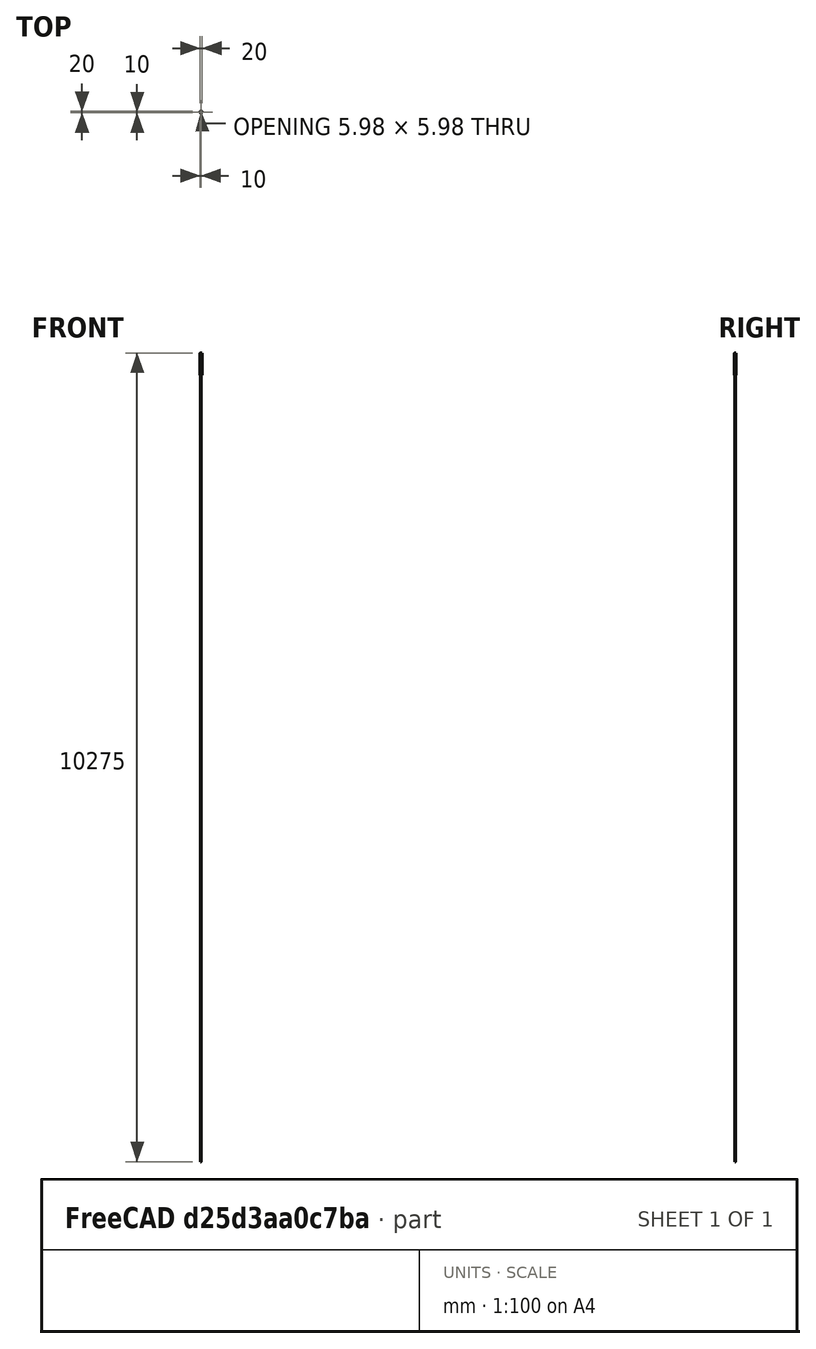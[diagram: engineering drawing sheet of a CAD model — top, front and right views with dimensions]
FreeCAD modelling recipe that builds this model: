
FCSTD DOCUMENT  (FreeCAD 0.15R4671 (Git))
Label: perfil 280mm
License: CC-BY 3.0
LicenseURL: http://creativecommons.org/licenses/by/3.0/
objects: Sketcher::SketchObject×2, Part::Extrusion×2, PartDesign::Pad×1, PartDesign::Pocket×1, App::MeasureDistance×1, Part::Cut×1
note: 9 computed .brp shape members not serialized (recipe doc carries the construction recipe); baked Part::Feature solids carry a one-line shape summary decoded from their .brp

FEATURE [Sketcher::SketchObject] Sketch
  Placement = pos=(1.5,0,0) rot=(0,0,1;0rad)
  sketch-geometry (136):
    g0: LineSegment StartX=0 StartY=20 StartZ=0 EndX=4.65 EndY=20 EndZ=0
    g1: ArcOfCircle CenterX=-1e-12 CenterY=18.5 CenterZ=0 NormalX=0 NormalY=0 NormalZ=1 Radius=1.5 StartAngle=1.5708 EndAngle=3.14159
    g2: LineSegment StartX=-1.5 StartY=13.85 StartZ=0 EndX=-1.5 EndY=18.5 EndZ=0
    g3: ArcOfCircle CenterX=-1.3 CenterY=13.85 CenterZ=0 NormalX=0 NormalY=0 NormalZ=1 Radius=0.2 StartAngle=3.14159 EndAngle=4.71239
    g4: LineSegment StartX=-1 StartY=13.65 StartZ=0 EndX=-1.3 EndY=13.65 EndZ=0
    g5: LineSegment StartX=-1 StartY=13.3 StartZ=0 EndX=-1 EndY=13.65 EndZ=0
    g6: ArcOfCircle CenterX=-0.8 CenterY=13.3 CenterZ=0 NormalX=0 NormalY=0 NormalZ=1 Radius=0.2 StartAngle=3.14159 EndAngle=4.71239
    g7: LineSegment StartX=-0.5 StartY=13.1 StartZ=0 EndX=-0.8 EndY=13.1 EndZ=0
    g8: ArcOfCircle CenterX=-0.5 CenterY=13.6 CenterZ=0 NormalX=0 NormalY=0 NormalZ=1 Radius=0.5 StartAngle=4.71239 EndAngle=6.28319
    g9: LineSegment StartX=2.68e-07 StartY=15.5 StartZ=0 EndX=2.68e-07 EndY=13.6 EndZ=0
    g10: ArcOfCircle CenterX=0.5 CenterY=15.5 CenterZ=0 NormalX=0 NormalY=0 NormalZ=1 Radius=0.5 StartAngle=1.5708 EndAngle=3.14159
    g11: LineSegment StartX=1.23223 StartY=16 StartZ=0 EndX=0.5 EndY=16 EndZ=0
    g12: ArcOfCircle CenterX=1.23223 CenterY=15.5 CenterZ=0 NormalX=0 NormalY=0 NormalZ=1 Radius=0.5 StartAngle=0.785398 EndAngle=1.5708
    g13: LineSegment StartX=3.85355 StartY=13.5858 StartZ=0 EndX=1.58579 EndY=15.8536 EndZ=0
    g14: ArcOfCircle CenterX=3.5 CenterY=13.2322 CenterZ=0 NormalX=0 NormalY=0 NormalZ=1 Radius=0.5 StartAngle=0 EndAngle=0.785398
    g15: LineSegment StartX=4 StartY=10.9536 StartZ=0 EndX=4 EndY=13.2322 EndZ=0
    g16: ArcOfCircle CenterX=4.2 CenterY=10.9536 CenterZ=0 NormalX=0 NormalY=0 NormalZ=1 Radius=0.2 StartAngle=3.14159 EndAngle=3.66519
    g17: LineSegment StartX=4.46188 StartY=10.1 StartZ=0 EndX=4.0268 EndY=10.8536 EndZ=0
    g18: ArcOfCircle CenterX=4.28868 CenterY=10 CenterZ=0 NormalX=0 NormalY=0 NormalZ=1 Radius=0.2 StartAngle=5.75959 EndAngle=6.80678
    g19: LineSegment StartX=4.0268 StartY=9.14641 StartZ=0 EndX=4.46188 EndY=9.9 EndZ=0
    g20: ArcOfCircle CenterX=4.2 CenterY=9.04641 CenterZ=0 NormalX=0 NormalY=0 NormalZ=1 Radius=0.2 StartAngle=2.61799 EndAngle=3.14159
    g21: LineSegment StartX=4 StartY=6.76777 StartZ=0 EndX=4 EndY=9.04641 EndZ=0
    g22: ArcOfCircle CenterX=3.5 CenterY=6.76777 CenterZ=0 NormalX=0 NormalY=0 NormalZ=1 Radius=0.5 StartAngle=5.49779 EndAngle=6.28319
    g23: LineSegment StartX=1.58579 StartY=4.14645 StartZ=0 EndX=3.85355 EndY=6.41421 EndZ=0
    g24: ArcOfCircle CenterX=1.23223 CenterY=4.5 CenterZ=0 NormalX=0 NormalY=0 NormalZ=1 Radius=0.5 StartAngle=4.71239 EndAngle=5.49779
    g25: LineSegment StartX=0.5 StartY=4 StartZ=0 EndX=1.23223 EndY=4 EndZ=0
    g26: ArcOfCircle CenterX=0.5 CenterY=4.5 CenterZ=0 NormalX=0 NormalY=0 NormalZ=1 Radius=0.5 StartAngle=3.14159 EndAngle=4.71239
    g27: LineSegment StartX=2.68e-07 StartY=6.4 StartZ=0 EndX=2.68e-07 EndY=4.5 EndZ=0
    g28: ArcOfCircle CenterX=-0.5 CenterY=6.4 CenterZ=0 NormalX=0 NormalY=0 NormalZ=1 Radius=0.5 StartAngle=0 EndAngle=1.5708
    g29: LineSegment StartX=-0.8 StartY=6.9 StartZ=0 EndX=-0.5 EndY=6.9 EndZ=0
    g30: ArcOfCircle CenterX=-0.8 CenterY=6.7 CenterZ=0 NormalX=0 NormalY=0 NormalZ=1 Radius=0.2 StartAngle=1.5708 EndAngle=3.14159
    g31: LineSegment StartX=-1 StartY=6.35 StartZ=0 EndX=-1 EndY=6.7 EndZ=0
    g32: LineSegment StartX=-1.3 StartY=6.35 StartZ=0 EndX=-1 EndY=6.35 EndZ=0
    g33: ArcOfCircle CenterX=-1.3 CenterY=6.15 CenterZ=0 NormalX=0 NormalY=0 NormalZ=1 Radius=0.2 StartAngle=1.5708 EndAngle=3.14159
    g34: LineSegment StartX=-1.5 StartY=1.5 StartZ=0 EndX=-1.5 EndY=6.15 EndZ=0
    g35: ArcOfCircle CenterX=0 CenterY=1.5 CenterZ=0 NormalX=0 NormalY=0 NormalZ=1 Radius=1.5 StartAngle=3.14159 EndAngle=4.71239
    g36: LineSegment StartX=4.65 StartY=1e-12 StartZ=0 EndX=0 EndY=0 EndZ=0
    g37: ArcOfCircle CenterX=4.65 CenterY=0.2 CenterZ=0 NormalX=0 NormalY=0 NormalZ=1 Radius=0.2 StartAngle=4.71239 EndAngle=6.28319
    g38: LineSegment StartX=4.85 StartY=0.5 StartZ=0 EndX=4.85 EndY=0.2 EndZ=0
    g39: LineSegment StartX=5.2 StartY=0.5 StartZ=0 EndX=4.85 EndY=0.5 EndZ=0
    g40: ArcOfCircle CenterX=5.2 CenterY=0.7 CenterZ=0 NormalX=0 NormalY=0 NormalZ=1 Radius=0.2 StartAngle=4.71239 EndAngle=6.28319
    g41: LineSegment StartX=5.4 StartY=1 StartZ=0 EndX=5.4 EndY=0.7 EndZ=0
    g42: ArcOfCircle CenterX=4.9 CenterY=1 CenterZ=0 NormalX=0 NormalY=0 NormalZ=1 Radius=0.5 StartAngle=0 EndAngle=1.5708
    g43: LineSegment StartX=3 StartY=1.5 StartZ=0 EndX=4.9 EndY=1.5 EndZ=0
    g44: ArcOfCircle CenterX=3 CenterY=2 CenterZ=0 NormalX=0 NormalY=0 NormalZ=1 Radius=0.5 StartAngle=3.14159 EndAngle=4.71239
    g45: LineSegment StartX=2.5 StartY=2.73223 StartZ=0 EndX=2.5 EndY=2 EndZ=0
    g46: ArcOfCircle CenterX=3 CenterY=2.73223 CenterZ=0 NormalX=0 NormalY=0 NormalZ=1 Radius=0.5 StartAngle=2.35619 EndAngle=3.14159
    g47: LineSegment StartX=4.91421 StartY=5.35355 StartZ=0 EndX=2.64645 EndY=3.08579 EndZ=0
    g48: ArcOfCircle CenterX=5.26777 CenterY=5 CenterZ=0 NormalX=0 NormalY=0 NormalZ=1 Radius=0.5 StartAngle=1.5708 EndAngle=2.35619
    g49: LineSegment StartX=7.54641 StartY=5.5 StartZ=0 EndX=5.26777 EndY=5.5 EndZ=0
    g50: ArcOfCircle CenterX=7.54641 CenterY=5.7 CenterZ=0 NormalX=0 NormalY=0 NormalZ=1 Radius=0.2 StartAngle=4.71239 EndAngle=5.23599
    g51: LineSegment StartX=8.4 StartY=5.96188 StartZ=0 EndX=7.64641 EndY=5.52679 EndZ=0
    g52: ArcOfCircle CenterX=8.5 CenterY=5.78868 CenterZ=0 NormalX=0 NormalY=0 NormalZ=1 Radius=0.2 StartAngle=1.0472 EndAngle=2.0944
    g53: LineSegment StartX=9.35359 StartY=5.52679 StartZ=0 EndX=8.6 EndY=5.96188 EndZ=0
    g54: ArcOfCircle CenterX=9.45359 CenterY=5.7 CenterZ=0 NormalX=0 NormalY=0 NormalZ=1 Radius=0.2 StartAngle=4.18879 EndAngle=4.71239
    g55: LineSegment StartX=11.7322 StartY=5.5 StartZ=0 EndX=9.45359 EndY=5.5 EndZ=0
    g56: ArcOfCircle CenterX=11.7322 CenterY=5 CenterZ=0 NormalX=0 NormalY=0 NormalZ=1 Radius=0.5 StartAngle=0.785398 EndAngle=1.5708
    g57: LineSegment StartX=14.3536 StartY=3.08579 StartZ=0 EndX=12.0858 EndY=5.35355 EndZ=0
    g58: ArcOfCircle CenterX=14 CenterY=2.73223 CenterZ=0 NormalX=0 NormalY=0 NormalZ=1 Radius=0.5 StartAngle=0 EndAngle=0.785398
    g59: LineSegment StartX=14.5 StartY=2 StartZ=0 EndX=14.5 EndY=2.73223 EndZ=0
    g60: ArcOfCircle CenterX=14 CenterY=2 CenterZ=0 NormalX=0 NormalY=0 NormalZ=1 Radius=0.5 StartAngle=4.71239 EndAngle=6.28319
    g61: LineSegment StartX=12.1 StartY=1.5 StartZ=0 EndX=14 EndY=1.5 EndZ=0
    g62: ArcOfCircle CenterX=12.1 CenterY=1 CenterZ=0 NormalX=0 NormalY=0 NormalZ=1 Radius=0.5 StartAngle=1.5708 EndAngle=3.14159
    g63: LineSegment StartX=11.6 StartY=0.7 StartZ=0 EndX=11.6 EndY=1 EndZ=0
    g64: ArcOfCircle CenterX=11.8 CenterY=0.7 CenterZ=0 NormalX=0 NormalY=0 NormalZ=1 Radius=0.2 StartAngle=3.14159 EndAngle=4.71239
    g65: LineSegment StartX=12.15 StartY=0.5 StartZ=0 EndX=11.8 EndY=0.5 EndZ=0
    g66: LineSegment StartX=12.15 StartY=0.2 StartZ=0 EndX=12.15 EndY=0.5 EndZ=0
    g67: ArcOfCircle CenterX=12.35 CenterY=0.2 CenterZ=0 NormalX=0 NormalY=0 NormalZ=1 Radius=0.2 StartAngle=3.14159 EndAngle=4.71239
    g68: LineSegment StartX=17 StartY=1e-12 StartZ=0 EndX=12.35 EndY=0 EndZ=0
    g69: ArcOfCircle CenterX=17 CenterY=1.5 CenterZ=0 NormalX=0 NormalY=0 NormalZ=1 Radius=1.5 StartAngle=4.71239 EndAngle=6.28319
    g70: LineSegment StartX=18.5 StartY=6.15 StartZ=0 EndX=18.5 EndY=1.5 EndZ=0
    g71: ArcOfCircle CenterX=18.3 CenterY=6.15 CenterZ=0 NormalX=0 NormalY=0 NormalZ=1 Radius=0.2 StartAngle=0 EndAngle=1.5708
    g72: LineSegment StartX=18 StartY=6.35 StartZ=0 EndX=18.3 EndY=6.35 EndZ=0
    g73: LineSegment StartX=18 StartY=6.7 StartZ=0 EndX=18 EndY=6.35 EndZ=0
    g74: ArcOfCircle CenterX=17.8 CenterY=6.7 CenterZ=0 NormalX=0 NormalY=0 NormalZ=1 Radius=0.2 StartAngle=0 EndAngle=1.5708
    g75: LineSegment StartX=17.5 StartY=6.9 StartZ=0 EndX=17.8 EndY=6.9 EndZ=0
    g76: ArcOfCircle CenterX=17.5 CenterY=6.4 CenterZ=0 NormalX=0 NormalY=0 NormalZ=1 Radius=0.5 StartAngle=1.5708 EndAngle=3.14159
    g77: LineSegment StartX=17 StartY=4.5 StartZ=0 EndX=17 EndY=6.4 EndZ=0
    g78: ArcOfCircle CenterX=16.5 CenterY=4.5 CenterZ=0 NormalX=0 NormalY=0 NormalZ=1 Radius=0.5 StartAngle=4.71239 EndAngle=6.28319
    g79: LineSegment StartX=15.7678 StartY=4 StartZ=0 EndX=16.5 EndY=4 EndZ=0
    g80: ArcOfCircle CenterX=15.7678 CenterY=4.5 CenterZ=0 NormalX=0 NormalY=0 NormalZ=1 Radius=0.5 StartAngle=3.92699 EndAngle=4.71239
    g81: LineSegment StartX=13.1464 StartY=6.41421 StartZ=0 EndX=15.4142 EndY=4.14645 EndZ=0
    g82: ArcOfCircle CenterX=13.5 CenterY=6.76777 CenterZ=0 NormalX=0 NormalY=0 NormalZ=1 Radius=0.5 StartAngle=3.14159 EndAngle=3.92699
    g83: LineSegment StartX=13 StartY=9.04641 StartZ=0 EndX=13 EndY=6.76777 EndZ=0
    g84: ArcOfCircle CenterX=12.8 CenterY=9.04641 CenterZ=0 NormalX=0 NormalY=0 NormalZ=1 Radius=0.2 StartAngle=0 EndAngle=0.523599
    g85: LineSegment StartX=12.5381 StartY=9.9 StartZ=0 EndX=12.9732 EndY=9.14641 EndZ=0
    g86: ArcOfCircle CenterX=12.7113 CenterY=10 CenterZ=0 NormalX=0 NormalY=0 NormalZ=1 Radius=0.2 StartAngle=2.61799 EndAngle=3.66519
    g87: LineSegment StartX=12.9732 StartY=10.8536 StartZ=0 EndX=12.5381 EndY=10.1 EndZ=0
    g88: ArcOfCircle CenterX=12.8 CenterY=10.9536 CenterZ=0 NormalX=0 NormalY=0 NormalZ=1 Radius=0.2 StartAngle=5.75959 EndAngle=6.28319
    g89: LineSegment StartX=13 StartY=13.2322 StartZ=0 EndX=13 EndY=10.9536 EndZ=0
    g90: ArcOfCircle CenterX=13.5 CenterY=13.2322 CenterZ=0 NormalX=0 NormalY=0 NormalZ=1 Radius=0.5 StartAngle=2.35619 EndAngle=3.14159
    g91: LineSegment StartX=15.4142 StartY=15.8536 StartZ=0 EndX=13.1464 EndY=13.5858 EndZ=0
    g92: ArcOfCircle CenterX=15.7678 CenterY=15.5 CenterZ=0 NormalX=0 NormalY=0 NormalZ=1 Radius=0.5 StartAngle=1.5708 EndAngle=2.35619
    g93: LineSegment StartX=16.5 StartY=16 StartZ=0 EndX=15.7678 EndY=16 EndZ=0
    g94: ArcOfCircle CenterX=16.5 CenterY=15.5 CenterZ=0 NormalX=0 NormalY=0 NormalZ=1 Radius=0.5 StartAngle=0 EndAngle=1.5708
    g95: LineSegment StartX=17 StartY=13.6 StartZ=0 EndX=17 EndY=15.5 EndZ=0
    g96: ArcOfCircle CenterX=17.5 CenterY=13.6 CenterZ=0 NormalX=0 NormalY=0 NormalZ=1 Radius=0.5 StartAngle=3.14159 EndAngle=4.71239
    g97: LineSegment StartX=17.8 StartY=13.1 StartZ=0 EndX=17.5 EndY=13.1 EndZ=0
    g98: ArcOfCircle CenterX=17.8 CenterY=13.3 CenterZ=0 NormalX=0 NormalY=0 NormalZ=1 Radius=0.2 StartAngle=4.71239 EndAngle=6.28319
    g99: LineSegment StartX=18 StartY=13.65 StartZ=0 EndX=18 EndY=13.3 EndZ=0
    g100: LineSegment StartX=18.3 StartY=13.65 StartZ=0 EndX=18 EndY=13.65 EndZ=0
    g101: ArcOfCircle CenterX=18.3 CenterY=13.85 CenterZ=0 NormalX=0 NormalY=0 NormalZ=1 Radius=0.2 StartAngle=4.71239 EndAngle=6.28319
    g102: LineSegment StartX=18.5 StartY=18.5 StartZ=0 EndX=18.5 EndY=13.85 EndZ=0
    g103: ArcOfCircle CenterX=17 CenterY=18.5 CenterZ=0 NormalX=0 NormalY=0 NormalZ=1 Radius=1.5 StartAngle=0 EndAngle=1.5708
    g104: LineSegment StartX=12.35 StartY=20 StartZ=0 EndX=17 EndY=20 EndZ=0
    g105: ArcOfCircle CenterX=12.35 CenterY=19.8 CenterZ=0 NormalX=0 NormalY=0 NormalZ=1 Radius=0.2 StartAngle=1.5708 EndAngle=3.14159
    g106: LineSegment StartX=12.15 StartY=19.5 StartZ=0 EndX=12.15 EndY=19.8 EndZ=0
    g107: LineSegment StartX=11.8 StartY=19.5 StartZ=0 EndX=12.15 EndY=19.5 EndZ=0
    g108: ArcOfCircle CenterX=11.8 CenterY=19.3 CenterZ=0 NormalX=0 NormalY=0 NormalZ=1 Radius=0.2 StartAngle=1.5708 EndAngle=3.14159
    g109: LineSegment StartX=11.6 StartY=19 StartZ=0 EndX=11.6 EndY=19.3 EndZ=0
    g110: ArcOfCircle CenterX=12.1 CenterY=19 CenterZ=0 NormalX=0 NormalY=0 NormalZ=1 Radius=0.5 StartAngle=3.14159 EndAngle=4.71239
    g111: LineSegment StartX=14 StartY=18.5 StartZ=0 EndX=12.1 EndY=18.5 EndZ=0
    g112: ArcOfCircle CenterX=14 CenterY=18 CenterZ=0 NormalX=0 NormalY=0 NormalZ=1 Radius=0.5 StartAngle=0 EndAngle=1.5708
    g113: LineSegment StartX=14.5 StartY=17.2678 StartZ=0 EndX=14.5 EndY=18 EndZ=0
    g114: ArcOfCircle CenterX=14 CenterY=17.2678 CenterZ=0 NormalX=0 NormalY=0 NormalZ=1 Radius=0.5 StartAngle=5.49779 EndAngle=6.28319
    g115: LineSegment StartX=12.0858 StartY=14.6464 StartZ=0 EndX=14.3536 EndY=16.9142 EndZ=0
    g116: ArcOfCircle CenterX=11.7322 CenterY=15 CenterZ=0 NormalX=0 NormalY=0 NormalZ=1 Radius=0.5 StartAngle=4.71239 EndAngle=5.49779
    g117: LineSegment StartX=9.45359 StartY=14.5 StartZ=0 EndX=11.7322 EndY=14.5 EndZ=0
    g118: ArcOfCircle CenterX=9.45359 CenterY=14.3 CenterZ=0 NormalX=0 NormalY=0 NormalZ=1 Radius=0.2 StartAngle=1.5708 EndAngle=2.0944
    g119: LineSegment StartX=8.6 StartY=14.0381 StartZ=0 EndX=9.35359 EndY=14.4732 EndZ=0
    g120: ArcOfCircle CenterX=8.5 CenterY=14.2113 CenterZ=0 NormalX=0 NormalY=0 NormalZ=1 Radius=0.2 StartAngle=4.18879 EndAngle=5.23599
    g121: LineSegment StartX=7.64641 StartY=14.4732 StartZ=0 EndX=8.4 EndY=14.0381 EndZ=0
    g122: ArcOfCircle CenterX=7.54641 CenterY=14.3 CenterZ=0 NormalX=0 NormalY=0 NormalZ=1 Radius=0.2 StartAngle=1.0472 EndAngle=1.5708
    g123: LineSegment StartX=5.26777 StartY=14.5 StartZ=0 EndX=7.54641 EndY=14.5 EndZ=0
    g124: ArcOfCircle CenterX=5.26777 CenterY=15 CenterZ=0 NormalX=0 NormalY=0 NormalZ=1 Radius=0.5 StartAngle=3.92699 EndAngle=4.71239
    g125: LineSegment StartX=2.64645 StartY=16.9142 StartZ=0 EndX=4.91421 EndY=14.6464 EndZ=0
    g126: ArcOfCircle CenterX=3 CenterY=17.2678 CenterZ=0 NormalX=0 NormalY=0 NormalZ=1 Radius=0.5 StartAngle=3.14159 EndAngle=3.92699
    g127: LineSegment StartX=2.5 StartY=18 StartZ=0 EndX=2.5 EndY=17.2678 EndZ=0
    g128: ArcOfCircle CenterX=3 CenterY=18 CenterZ=0 NormalX=0 NormalY=0 NormalZ=1 Radius=0.5 StartAngle=1.5708 EndAngle=3.14159
    g129: LineSegment StartX=4.9 StartY=18.5 StartZ=0 EndX=3 EndY=18.5 EndZ=0
    g130: ArcOfCircle CenterX=4.9 CenterY=19 CenterZ=0 NormalX=0 NormalY=0 NormalZ=1 Radius=0.5 StartAngle=4.71239 EndAngle=6.28319
    g131: LineSegment StartX=5.4 StartY=19.3 StartZ=0 EndX=5.4 EndY=19 EndZ=0
    g132: ArcOfCircle CenterX=5.2 CenterY=19.3 CenterZ=0 NormalX=0 NormalY=0 NormalZ=1 Radius=0.2 StartAngle=0 EndAngle=1.5708
    g133: LineSegment StartX=4.85 StartY=19.5 StartZ=0 EndX=5.2 EndY=19.5 EndZ=0
    g134: LineSegment StartX=4.85 StartY=19.8 StartZ=0 EndX=4.85 EndY=19.5 EndZ=0
    g135: ArcOfCircle CenterX=4.65 CenterY=19.8 CenterZ=0 NormalX=0 NormalY=0 NormalZ=1 Radius=0.2 StartAngle=0 EndAngle=1.5708
  constraints (136):
    c: Coincident(g0,g1)
    c: Coincident(g135,g0)
    c: Coincident(g1,g2)
    c: Coincident(g2,g3)
    c: Coincident(g3,g4)
    c: Coincident(g4,g5)
    c: Coincident(g6,g5)
    c: Coincident(g7,g6)
    c: Coincident(g8,g7)
    c: Coincident(g9,g8)
    c: Coincident(g10,g9)
    c: Coincident(g10,g11)
    c: Coincident(g11,g12)
    c: Coincident(g12,g13)
    c: Coincident(g14,g13)
    c: Coincident(g15,g14)
    c: Coincident(g15,g16)
    c: Coincident(g16,g17)
    c: Coincident(g17,g18)
    c: Coincident(g18,g19)
    c: Coincident(g19,g20)
    c: Coincident(g20,g21)
    c: Coincident(g21,g22)
    c: Coincident(g22,g23)
    c: Coincident(g23,g24)
    c: Coincident(g24,g25)
    c: Coincident(g26,g25)
    c: Coincident(g26,g27)
    c: Coincident(g28,g27)
    c: Coincident(g28,g29)
    c: Coincident(g30,g29)
    c: Coincident(g31,g30)
    c: Coincident(g31,g32)
    c: Coincident(g32,g33)
    c: Coincident(g33,g34)
    c: Coincident(g35,g34)
    c: Coincident(g36,g35)
    c: Coincident(g37,g36)
    c: Coincident(g37,g38)
    c: Coincident(g38,g39)
    c: Coincident(g40,g39)
    c: Coincident(g40,g41)
    c: Coincident(g41,g42)
    c: Coincident(g43,g42)
    c: Coincident(g44,g43)
    c: Coincident(g44,g45)
    c: Coincident(g45,g46)
    c: Coincident(g46,g47)
    c: Coincident(g47,g48)
    c: Coincident(g49,g48)
    c: Coincident(g49,g50)
    c: Coincident(g50,g51)
    c: Coincident(g51,g52)
    c: Coincident(g53,g52)
    c: Coincident(g54,g53)
    c: Coincident(g55,g54)
    c: Coincident(g56,g55)
    c: Coincident(g56,g57)
    c: Coincident(g58,g57)
    c: Coincident(g59,g58)
    c: Coincident(g60,g59)
    c: Coincident(g61,g60)
    c: Coincident(g62,g61)
    c: Coincident(g62,g63)
    c: Coincident(g64,g63)
    c: Coincident(g65,g64)
    c: Coincident(g66,g65)
    c: Coincident(g67,g66)
    c: Coincident(g67,g68)
    c: Coincident(g69,g68)
    c: Coincident(g70,g69)
    c: Coincident(g71,g70)
    c: Coincident(g72,g71)
    c: Coincident(g73,g72)
    c: Coincident(g73,g74)
    c: Coincident(g75,g74)
    c: Coincident(g76,g75)
    c: Coincident(g76,g77)
    c: Coincident(g77,g78)
    c: Coincident(g78,g79)
    c: Coincident(g80,g79)
    c: Coincident(g81,g80)
    c: Coincident(g81,g82)
    c: Coincident(g82,g83)
    c: Coincident(g83,g84)
    c: Coincident(g85,g84)
    c: Coincident(g86,g85)
    c: Coincident(g86,g87)
    c: Coincident(g88,g87)
    c: Coincident(g88,g89)
    c: Coincident(g89,g90)
    c: Coincident(g91,g90)
    c: Coincident(g92,g91)
    c: Coincident(g93,g92)
    c: Coincident(g94,g93)
    c: Coincident(g94,g95)
    c: Coincident(g95,g96)
    c: Coincident(g96,g97)
    c: Coincident(g98,g97)
    c: Coincident(g98,g99)
    c: Coincident(g100,g99)
    c: Coincident(g100,g101)
    c: Coincident(g101,g102)
    c: Coincident(g102,g103)
    c: Coincident(g103,g104)
    c: Coincident(g104,g105)
    c: Coincident(g106,g105)
    c: Coincident(g107,g106)
    c: Coincident(g108,g107)
    c: Coincident(g109,g108)
    c: Coincident(g110,g109)
    c: Coincident(g111,g110)
    c: Coincident(g112,g111)
    c: Coincident(g112,g113)
    c: Coincident(g113,g114)
    c: Coincident(g114,g115)
    c: Coincident(g115,g116)
    c: Coincident(g117,g116)
    c: Coincident(g118,g117)
    c: Coincident(g119,g118)
    c: Coincident(g119,g120)
    c: Coincident(g121,g120)
    c: Coincident(g121,g122)
    c: Coincident(g122,g123)
    c: Coincident(g124,g123)
    c: Coincident(g124,g125)
    c: Coincident(g126,g125)
    c: Coincident(g127,g126)
    c: Coincident(g128,g127)
    c: Coincident(g129,g128)
    c: Coincident(g130,g129)
    c: Coincident(g130,g131)
    c: Coincident(g131,g132)
    c: Coincident(g133,g132)
    c: Coincident(g134,g133)
    c: Coincident(g135,g134)
FEATURE [PartDesign::Pad] Pad
  Length = 5
  Length2 = 100
  Placement = pos=(1.5,0,0) rot=(0,0,1;0rad)
  Sketch = -> Sketch
  Type = 0
FEATURE [Sketcher::SketchObject] Sketch001
  Placement = pos=(1.5,0,5) rot=(0,0,1;0rad)
  Support = -> Pad [Face138]
  sketch-geometry (16):
    g0: ArcOfCircle CenterX=8.5 CenterY=10 CenterZ=0 NormalX=0 NormalY=0 NormalZ=1 Radius=3.54978 StartAngle=2.14023 EndAngle=2.57348
    g1: LineSegment StartX=6.5861 StartY=12.9896 StartZ=0 EndX=7.24181 EndY=12.4453 EndZ=0
    g2: ArcOfCircle CenterX=8.5 CenterY=10 CenterZ=0 NormalX=0 NormalY=0 NormalZ=1 Radius=2.75 StartAngle=1.09559 EndAngle=2.046
    g3: LineSegment StartX=9.75819 StartY=12.4453 StartZ=0 EndX=10.4139 EndY=12.9896 EndZ=0
    g4: ArcOfCircle CenterX=8.5 CenterY=10 CenterZ=0 NormalX=0 NormalY=0 NormalZ=1 Radius=3.54978 StartAngle=0.568112 EndAngle=1.00136
    g5: LineSegment StartX=11.4922 StartY=11.9099 StartZ=0 EndX=10.9453 EndY=11.2582 EndZ=0
    g6: ArcOfCircle CenterX=8.5 CenterY=10 CenterZ=0 NormalX=0 NormalY=0 NormalZ=1 Radius=2.75 StartAngle=5.80798 EndAngle=6.75839
    g7: LineSegment StartX=10.9453 StartY=8.74181 StartZ=0 EndX=11.4922 EndY=8.09007 EndZ=0
    g8: ArcOfCircle CenterX=8.5 CenterY=10 CenterZ=0 NormalX=0 NormalY=0 NormalZ=1 Radius=3.54978 StartAngle=5.28183 EndAngle=5.71507
    g9: LineSegment StartX=10.4139 StartY=7.01036 StartZ=0 EndX=9.75819 EndY=7.5547 EndZ=0
    g10: ArcOfCircle CenterX=8.5 CenterY=10 CenterZ=0 NormalX=0 NormalY=0 NormalZ=1 Radius=2.75 StartAngle=4.23718 EndAngle=5.1876
    g11: LineSegment StartX=7.24181 StartY=7.5547 StartZ=0 EndX=6.5861 EndY=7.01036 EndZ=0
    g12: ArcOfCircle CenterX=8.5 CenterY=10 CenterZ=0 NormalX=0 NormalY=0 NormalZ=1 Radius=3.54978 StartAngle=3.7097 EndAngle=4.14295
    g13: LineSegment StartX=5.50783 StartY=8.09007 StartZ=0 EndX=6.0547 EndY=8.74181 EndZ=0
    g14: ArcOfCircle CenterX=8.5 CenterY=10 CenterZ=0 NormalX=0 NormalY=0 NormalZ=1 Radius=2.75 StartAngle=2.66639 EndAngle=3.6168
    g15: LineSegment StartX=6.0547 StartY=11.2582 StartZ=0 EndX=5.50783 EndY=11.9099 EndZ=0
  constraints (16):
    c: Coincident(g0,g1)
    c: Coincident(g15,g0)
    c: Coincident(g1,g2)
    c: Coincident(g3,g2)
    c: Coincident(g4,g3)
    c: Coincident(g4,g5)
    c: Coincident(g6,g5)
    c: Coincident(g7,g6)
    c: Coincident(g8,g7)
    c: Coincident(g9,g8)
    c: Coincident(g10,g9)
    c: Coincident(g11,g10)
    c: Coincident(g12,g11)
    c: Coincident(g13,g12)
    c: Coincident(g14,g13)
    c: Coincident(g15,g14)
FEATURE [PartDesign::Pocket] Pocket
  Length = 5
  Placement = pos=(1.5,0,0) rot=(0,0,1;0rad)
  Sketch = -> Sketch001
  Type = 1
FEATURE [Part::Extrusion] Extrude001
  Base = -> Sketch001
  Dir = (0,0,470)
  Placement = pos=(0,0,-25) rot=(0,0,1;0rad)
  Solid = true
FEATURE [Part::Extrusion] Extrude
  Base = -> Sketch
  Dir = (0,0,280)
  Solid = true
FEATURE [App::MeasureDistance] Distance  label="Distance: 280.000"
  Distance = 280
  P1 = (0.200962,0.75,280)
  P2 = (0.084175,1.00458,0)
FEATURE [Part::Cut] Cut
  Base = -> Extrude
  Tool = -> Extrude001
